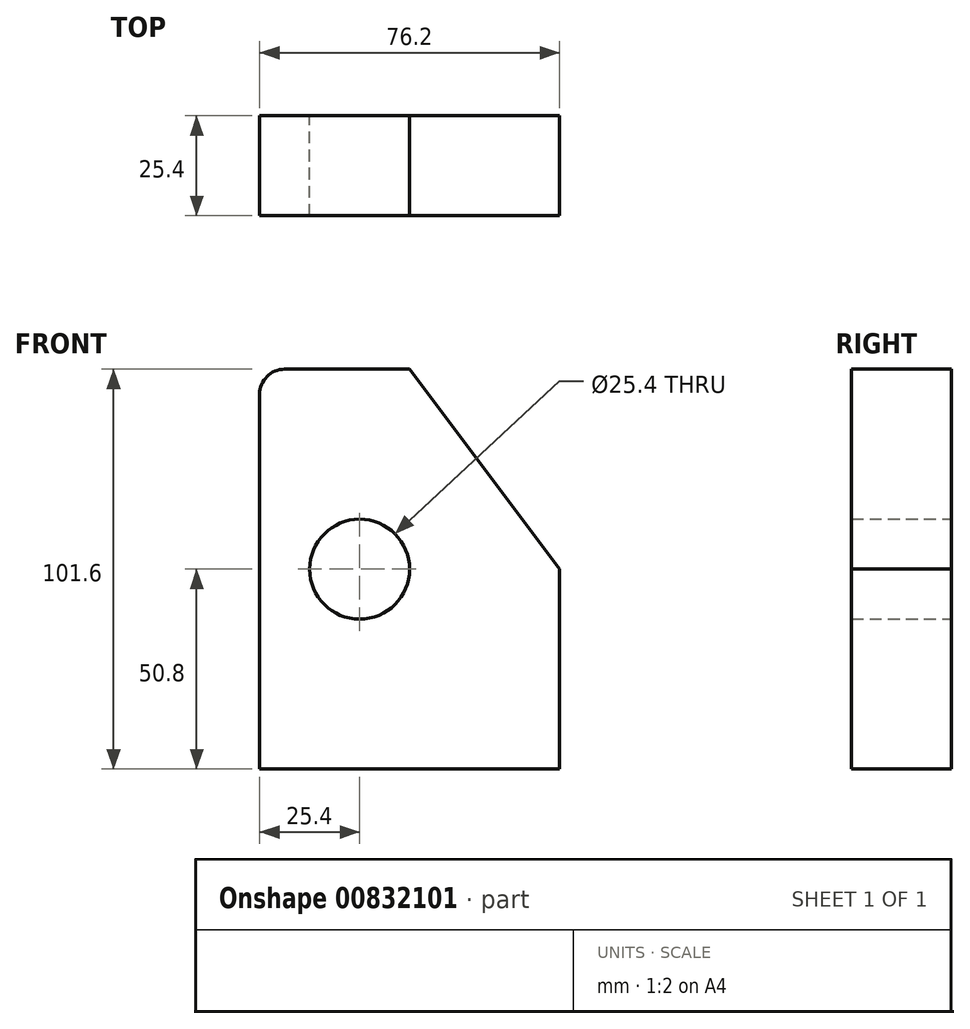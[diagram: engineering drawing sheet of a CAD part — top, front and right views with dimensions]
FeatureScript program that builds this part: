
annotation { "Feature Type Name" : "Feature", "Feature Type Description" : "" }
export const myFeature = defineFeature(function(context is Context, id is Id, definition is map)
    precondition{}
    {
        {
            var Q0;
            Q0=qCreatedBy(makeId("Front.planeOp"),FACE);
            var sketch = newSketch(context, id + "F0", { "sketchPlane" : qUnion([Q0])});
            skLineSegment(sketch, "E0.bottom", {"start": v(-31.75, 50.8) * mm, "end": v(38.1, 50.8) * mm});
            skLineSegment(sketch, "E0.top", {"start": v(-38.1, -50.8) * mm, "end": v(38.1, -50.8) * mm});
            skLineSegment(sketch, "E0.left", {"start": v(-38.1, 44.45) * mm, "end": v(-38.1, -50.8) * mm});
            skLineSegment(sketch, "E0.right", {"start": v(38.1, 50.8) * mm, "end": v(38.1, -50.8) * mm});
            skLineSegment(sketch, "E1", {"start": v(0, 50.8) * mm, "end": v(38.1, 0) * mm});
            skCircle(sketch, "E2", {"center": v(-12.7, 0) * mm, "radius": 12.7 * mm});
            skPoint(sketch, "E3.visualSharp", {"position": v(-38.1, 50.8) * mm});
            skArc(sketch, "E3.filletArc", {"start": v(-31.75, 50.8) * mm, "mid": v(-36.24, 48.94) * mm, "end": v(-38.1, 44.45) * mm});
            skSolve(sketch);
        }
        {
            var Q0;
            {var subQ0=sQuery(id+"F0.wireOp",EDGE,"E0.top");Q0=makeQuery(id+"F0.imprint","IMPRINT",FACE,{"disambiguationData":[TD([[makeQuery(id+"F0.imprint","IMPRINT",EDGE,{"derivedFrom":subQ0}),1.0]])]});}
            extrude(context, id + "F1", {"entities" : qUnion([Q0]), "depth" : 25.4 * mm, "offsetDistance" : 25.4 * mm});
        }
    });
